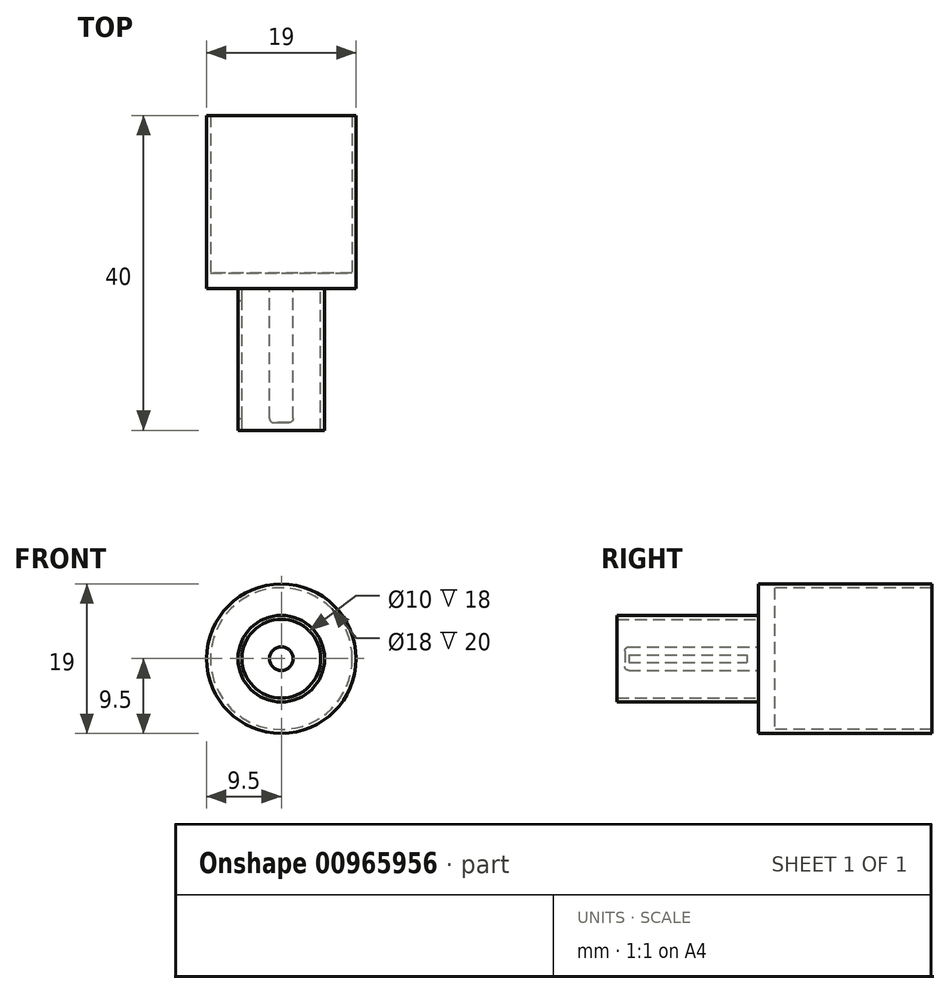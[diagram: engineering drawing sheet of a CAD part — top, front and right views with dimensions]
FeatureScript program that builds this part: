
annotation { "Feature Type Name" : "Feature", "Feature Type Description" : "" }
export const myFeature = defineFeature(function(context is Context, id is Id, definition is map)
    precondition{}
    {
        {
            var Q0;
            Q0=qCreatedBy(makeId("Front.planeOp"),FACE);
            var sketch = newSketch(context, id + "F0", { "sketchPlane" : qUnion([Q0])});
            skCircle(sketch, "E0", {"center": v(0, 0) * mm, "radius": 5.5 * mm});
            skCircle(sketch, "E1", {"center": v(0, 0) * mm, "radius": 5 * mm});
            skSolve(sketch);
        }
        {
            var Q0;
            Q0=makeQuery(id+"F0.imprint","IMPRINT",FACE,{"disambiguationData":[TD([[makeQuery(id+"F0.imprint","IMPRINT",EDGE,{"derivedFrom":sQuery(id+"F0.wireOp",EDGE,"E0")}),1.0]])]});
            extrude(context, id + "F1", {"entities" : qUnion([Q0]), "depth" : 35 * mm, "offsetDistance" : 25 * mm});
        }
        {
            var Q0;
            Q0=qCreatedBy(makeId("Top.planeOp"),FACE);
            var sketch = newSketch(context, id + "F2", { "sketchPlane" : qUnion([Q0])});
            skLineSegment(sketch, "E2.bottom", {"start": v(-9, -15) * mm, "end": v(9, -15) * mm});
            skLineSegment(sketch, "E2.top", {"start": v(-9, 15) * mm, "end": v(9, 15) * mm});
            skLineSegment(sketch, "E2.left", {"start": v(-9, -15) * mm, "end": v(-9, 15) * mm});
            skLineSegment(sketch, "E2.right", {"start": v(9, -15) * mm, "end": v(9, 15) * mm});
            skPoint(sketch, "E2.middle", {"position": v(0, 0) * mm});
            skSolve(sketch);
        }
        {
            var Q0;
            Q0=makeQuery(id+"F2.imprint","IMPRINT",FACE,{"disambiguationData":[TD([[makeQuery(id+"F2.imprint","IMPRINT",EDGE,{"derivedFrom":sQuery(id+"F2.wireOp",EDGE,"E2.bottom")}),1.0]])]});
            extrude(context, id + "F3", {"entities" : qUnion([Q0]), "operationType" : NewBodyOperationType.REMOVE, "depth" : 25 * mm, "offsetDistance" : 25 * mm, "hasSecondDirection" : true, "secondDirectionOppositeDirection" : true, "secondDirectionDepth" : 25 * mm});
        }
        {
            var Q0;
            Q0=makeQuery(id+"FK9VsIfb33r3V2G_1.boolean.opBoolean","MERGE",FACE,{"derivedFrom":[makeQuery(id+"F3.boolean.opBoolean","COPY",FACE,{"derivedFrom":makeQuery(id+"F3.opExtrude","SWEPT_FACE",FACE,{"disambiguationData":[OSD([sQuery(id+"F2.wireOp",EDGE,"E2.bottom")])]})})],"fromTools":[makeQuery(id+"FK9VsIfb33r3V2G_1.opExtrude","SWEPT_FACE",FACE,{"disambiguationData":[OSD([sQuery(id+"F9BlCA5kWQAFzgD_1.wireOp",EDGE,"xuU5gq9y-jPHS-n6Cl-S5eU-GhHB31Oq1M6Z.bottom")])]}),makeQuery(id+"FK9VsIfb33r3V2G_1.opExtrude","SWEPT_FACE",FACE,{"disambiguationData":[OSD([sQuery(id+"F9BlCA5kWQAFzgD_1.wireOp",EDGE,"zs8KGrtK-nU53-wOYU-HYpO-sikS8LrCLYJM.bottom")])]})]});
            var sketch = newSketch(context, id + "F4", { "sketchPlane" : qUnion([Q0])});
            skCircle(sketch, "E3.0", {"center": v(0, 0) * mm, "radius": 5.5 * mm});
            skCircle(sketch, "E4", {"center": v(0, 0) * mm, "radius": 7.5 * mm});
            skSolve(sketch);
        }
        {
            var Q0;
            Q0=makeQuery(id+"F4.imprint","IMPRINT",FACE,{"disambiguationData":[TD([[makeQuery(id+"F4.imprint","IMPRINT",EDGE,{"derivedFrom":sQuery(id+"F4.wireOp",EDGE,"E4")}),1.0]])]});
            var Q1;
            Q1=makeQuery(id+"F4.imprint","IMPRINT",FACE,{"disambiguationData":[TD([[makeQuery(id+"F4.imprint","IMPRINT",EDGE,{"derivedFrom":makeQuery(id+"F3.boolean.opBoolean","INTERSECT",EDGE,{"derivedFrom":[makeQuery(id+"F1.opExtrude","SWEPT_FACE",FACE,{"disambiguationData":[OSD([sQuery(id+"F0.wireOp",EDGE,"E1")])]}),makeQuery(id+"F3.opExtrude","SWEPT_FACE",FACE,{"disambiguationData":[OSD([sQuery(id+"F2.wireOp",EDGE,"E2.bottom")])]})]})}),1.0]])]});
            extrude(context, id + "F5", {"entities" : qUnion([Q0, Q1]), "operationType" : NewBodyOperationType.ADD, "oppositeDirection" : true, "depth" : 2 * mm, "offsetDistance" : 25 * mm});
        }
        {
            var Q0;
            Q0=qCreatedBy(makeId("Right.planeOp"),FACE);
            var sketch = newSketch(context, id + "F6", { "sketchPlane" : qUnion([Q0])});
            skLineSegment(sketch, "E5.bottom", {"start": v(-18.5, 0.5) * mm, "end": v(-33.5, 0.5) * mm});
            skLineSegment(sketch, "E5.top", {"start": v(-18.5, -0.5) * mm, "end": v(-33.5, -0.5) * mm});
            skLineSegment(sketch, "E5.left", {"start": v(-18.5, 0.5) * mm, "end": v(-18.5, -0.5) * mm});
            skLineSegment(sketch, "E5.right", {"start": v(-33.5, 0.5) * mm, "end": v(-33.5, -0.5) * mm});
            skSolve(sketch);
        }
        {
            var Q0;
            Q0 = qSketchRegion(id + "F6", true);
            extrude(context, id + "F7", {"entities" : qUnion([Q0]), "operationType" : NewBodyOperationType.REMOVE, "oppositeDirection" : true, "depth" : 10 * mm, "offsetDistance" : 25 * mm});
        }
        {
            var Q0;
            Q0=makeQuery(id+"F5.boolean.opBoolean","MERGE",FACE,{"derivedFrom":[makeQuery(id+"F3.boolean.opBoolean","COPY",FACE,{"derivedFrom":makeQuery(id+"F3.opExtrude","SWEPT_FACE",FACE,{"disambiguationData":[OSD([sQuery(id+"F2.wireOp",EDGE,"E2.bottom")])]})}),makeQuery(id+"F5.opExtrude","CAP_FACE",FACE,{"disambiguationData":[OSD([sQuery(id+"F4.wireOp",EDGE,"E3.0"),sQuery(id+"F4.wireOp",EDGE,"E4")])],"isStart":true})]});
            var sketch = newSketch(context, id + "F8", { "sketchPlane" : qUnion([Q0])});
            skCircle(sketch, "E6", {"center": v(0, 0) * mm, "radius": 5 * mm});
            skCircle(sketch, "E7", {"center": v(0, 0) * mm, "radius": 1.5 * mm});
            skSolve(sketch);
        }
        {
            var Q0;
            Q0=makeQuery(id+"F8.imprint","IMPRINT",FACE,{"disambiguationData":[TD([[makeQuery(id+"F8.imprint","IMPRINT",EDGE,{"derivedFrom":sQuery(id+"F8.wireOp",EDGE,"E7")}),1.0]])]});
            extrude(context, id + "F9", {"entities" : qUnion([Q0]), "operationType" : NewBodyOperationType.ADD, "oppositeDirection" : true, "depth" : 19 * mm, "offsetDistance" : 25 * mm});
        }
        {
            var Q0;
            {var subQ0=sQuery(id+"F2.wireOp",EDGE,"E2.bottom");Q0=makeQuery(id+"F5.boolean.opBoolean","MERGE",FACE,{"derivedFrom":[makeQuery(id+"F3.boolean.opBoolean","COPY",FACE,{"derivedFrom":makeQuery(id+"F3.opExtrude","SWEPT_FACE",FACE,{"disambiguationData":[OSD([subQ0])]})}),makeQuery(id+"F5.opExtrude","CAP_FACE",FACE,{"disambiguationData":[OSD([sQuery(id+"F4.wireOp",EDGE,"E3.0"),sQuery(id+"F4.wireOp",EDGE,"E4")])],"isStart":true}),makeQuery(id+"F5.opExtrude","CAP_FACE",FACE,{"disambiguationData":[OSD([sQuery(id+"F0.wireOp",EDGE,"E1"),subQ0])],"isStart":true})]});}
            var sketch = newSketch(context, id + "F10", { "sketchPlane" : qUnion([Q0])});
            skSolve(sketch);
        }
        {
            var Q0;
            Q0=makeQuery(id+"F10.imprint","IMPRINT",FACE,{"disambiguationData":[TD([[makeQuery(id+"F10.imprint","IMPRINT",EDGE,{"derivedFrom":makeQuery(id+"F5.opExtrude","CAP_EDGE",EDGE,{"disambiguationData":[OSD([sQuery(id+"F4.wireOp",EDGE,"E4")])],"isStart":true})}),1.0]])]});
            var sketch = newSketch(context, id + "F11", { "sketchPlane" : qUnion([Q0])});
            skCircle(sketch, "E8", {"center": v(0, 0) * mm, "radius": 9 * mm});
            skCircle(sketch, "E9", {"center": v(0, 0) * mm, "radius": 9.5 * mm});
            skSolve(sketch);
        }
        {
            var Q0;
            Q0=makeQuery(id+"F11.imprint","IMPRINT",FACE,{"disambiguationData":[TD([[makeQuery(id+"F11.imprint","IMPRINT",EDGE,{"derivedFrom":sQuery(id+"F11.wireOp",EDGE,"E8")}),1.0]])]});
            var Q1;
            Q1=makeQuery(id+"F11.imprint","IMPRINT",FACE,{"disambiguationData":[TD([[makeQuery(id+"F11.imprint","IMPRINT",EDGE,{"derivedFrom":sQuery(id+"F11.wireOp",EDGE,"E8")}),-1.0]])]});
            extrude(context, id + "F12", {"entities" : qUnion([Q0, Q1]), "operationType" : NewBodyOperationType.ADD, "oppositeDirection" : true, "depth" : 2 * mm, "offsetDistance" : 25 * mm});
        }
        {
            var Q0;
            Q0=makeQuery(id+"F11.imprint","IMPRINT",FACE,{"disambiguationData":[TD([[makeQuery(id+"F11.imprint","IMPRINT",EDGE,{"derivedFrom":sQuery(id+"F11.wireOp",EDGE,"E8")}),-1.0]])]});
            extrude(context, id + "F13", {"entities" : qUnion([Q0]), "operationType" : NewBodyOperationType.ADD, "depth" : 20 * mm, "offsetDistance" : 25 * mm});
        }
        {
            var Q0;
            Q0=makeQuery(id+"F9.opExtrude","CAP_EDGE",EDGE,{"disambiguationData":[OSD([sQuery(id+"F8.wireOp",EDGE,"E7")])],"isStart":false});
            fillet(context, id + "F14", {"entities" : qUnion([Q0]), "radius" : .5 * mm, "tangentPropagation" : true, "allowEdgeOverflow" : false});
        }
    });
